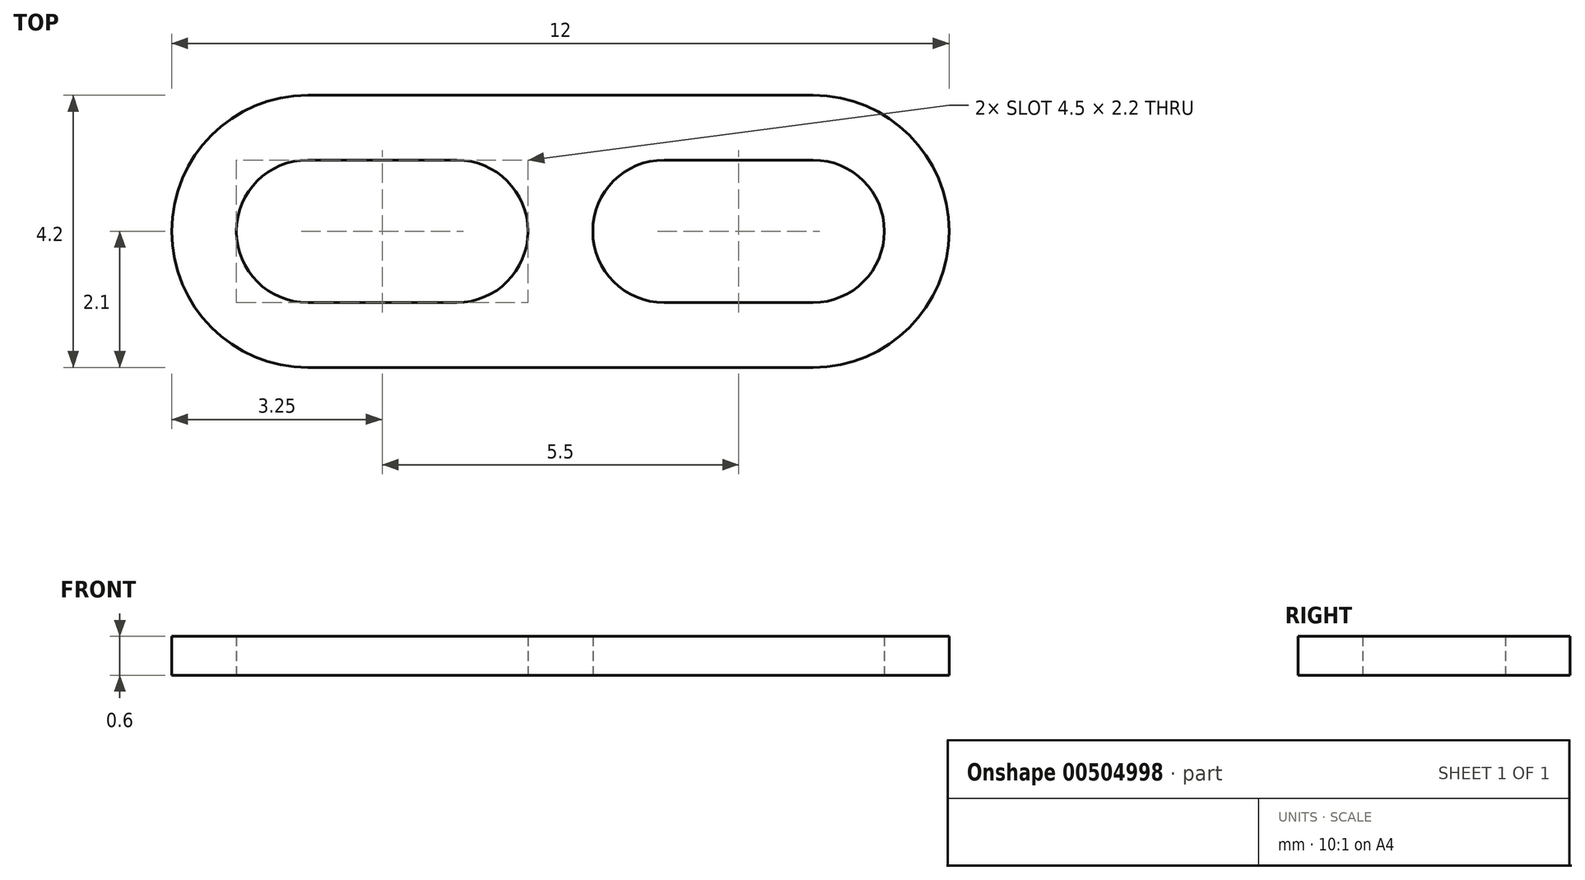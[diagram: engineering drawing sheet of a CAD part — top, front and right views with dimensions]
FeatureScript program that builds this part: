
annotation { "Feature Type Name" : "Feature", "Feature Type Description" : "" }
export const myFeature = defineFeature(function(context is Context, id is Id, definition is map)
    precondition{}
    {
        {
            var Q0;
            Q0=qCreatedBy(makeId("Top.planeOp"),FACE);
            var sketch = newSketch(context, id + "F0", { "sketchPlane" : qUnion([Q0])});
            skLineSegment(sketch, "E0.bottom", {"start": v(-3.9, 2) * mm, "end": v(3.9, 2) * mm});
            skLineSegment(sketch, "E0.top", {"start": v(-3.9, -2.2) * mm, "end": v(3.9, -2.2) * mm});
            skLineSegment(sketch, "E0.left", {"start": v(-6, -0.1) * mm, "end": v(-6, -0.1) * mm});
            skLineSegment(sketch, "E0.right", {"start": v(6, -0.1) * mm, "end": v(6, -0.1) * mm});
            skPoint(sketch, "E0.middle", {"position": v(0, 0) * mm});
            skPoint(sketch, "E1.visualSharp", {"position": v(-6, 2) * mm});
            skLineSegment(sketch, "E1.filletArc", {"start": v(-6, 2) * mm, "end": v(-6, 2) * mm});
            skLineSegment(sketch, "E2.filletArc", {"start": v(-6, -2.2) * mm, "end": v(-6, -2.2) * mm});
            skPoint(sketch, "E3.visualSharp", {"position": v(6, 2) * mm});
            skLineSegment(sketch, "E3.filletArc", {"start": v(6, 2) * mm, "end": v(6, 2) * mm});
            skLineSegment(sketch, "E4.filletArc", {"start": v(6, -2.2) * mm, "end": v(6, -2.2) * mm});
            skLineSegment(sketch, "E5.bottom", {"start": v(-3.9, 1) * mm, "end": v(-1.6, 1) * mm});
            skLineSegment(sketch, "E5.top", {"start": v(-3.9, -1.2) * mm, "end": v(-1.6, -1.2) * mm});
            skLineSegment(sketch, "E5.left", {"start": v(-5, -0.1) * mm, "end": v(-5, -0.1) * mm});
            skLineSegment(sketch, "E5.right", {"start": v(-0.5, -0.1) * mm, "end": v(-0.5, -0.1) * mm});
            skLineSegment(sketch, "E6.bottom", {"start": v(1.6, 1) * mm, "end": v(3.9, 1) * mm});
            skLineSegment(sketch, "E6.top", {"start": v(1.6, -1.2) * mm, "end": v(3.9, -1.2) * mm});
            skLineSegment(sketch, "E6.left", {"start": v(0.5, -0.1) * mm, "end": v(0.5, -0.1) * mm});
            skLineSegment(sketch, "E6.right", {"start": v(5, -0.1) * mm, "end": v(5, -0.1) * mm});
            skPoint(sketch, "E7.visualSharp", {"position": v(-5, 1) * mm});
            skArc(sketch, "E7.filletArc", {"start": v(-3.9, 1) * mm, "mid": v(-4.68, 0.68) * mm, "end": v(-5, -0.1) * mm});
            skPoint(sketch, "E8.visualSharp", {"position": v(-5, -1.2) * mm});
            skArc(sketch, "E8.filletArc", {"start": v(-5, -0.1) * mm, "mid": v(-4.68, -0.88) * mm, "end": v(-3.9, -1.2) * mm});
            skPoint(sketch, "E9.visualSharp", {"position": v(-0.5, -1.2) * mm});
            skArc(sketch, "E9.filletArc", {"start": v(-1.6, -1.2) * mm, "mid": v(-0.82, -0.88) * mm, "end": v(-0.5, -0.1) * mm});
            skPoint(sketch, "E10.visualSharp", {"position": v(-0.5, 1) * mm});
            skArc(sketch, "E10.filletArc", {"start": v(-0.5, -0.1) * mm, "mid": v(-0.82, 0.68) * mm, "end": v(-1.6, 1) * mm});
            skPoint(sketch, "E11.visualSharp", {"position": v(0.5, 1) * mm});
            skArc(sketch, "E11.filletArc", {"start": v(1.6, 1) * mm, "mid": v(0.82, 0.68) * mm, "end": v(0.5, -0.1) * mm});
            skPoint(sketch, "E12.visualSharp", {"position": v(0.5, -1.2) * mm});
            skArc(sketch, "E12.filletArc", {"start": v(0.5, -0.1) * mm, "mid": v(0.82, -0.88) * mm, "end": v(1.6, -1.2) * mm});
            skPoint(sketch, "E13.visualSharp", {"position": v(5, 1) * mm});
            skArc(sketch, "E13.filletArc", {"start": v(5, -0.1) * mm, "mid": v(4.68, 0.68) * mm, "end": v(3.9, 1) * mm});
            skPoint(sketch, "E14.visualSharp", {"position": v(5, -1.2) * mm});
            skArc(sketch, "E14.filletArc", {"start": v(3.9, -1.2) * mm, "mid": v(4.68, -0.88) * mm, "end": v(5, -0.1) * mm});
            skArc(sketch, "E15.filletArc", {"start": v(-3.9, 2) * mm, "mid": v(-5.38, 1.38) * mm, "end": v(-6, -0.1) * mm});
            skArc(sketch, "E16.filletArc", {"start": v(-6, -0.1) * mm, "mid": v(-5.38, -1.58) * mm, "end": v(-3.9, -2.2) * mm});
            skArc(sketch, "E17.filletArc", {"start": v(6, -0.1) * mm, "mid": v(5.38, 1.38) * mm, "end": v(3.9, 2) * mm});
            skArc(sketch, "E18.filletArc", {"start": v(3.9, -2.2) * mm, "mid": v(5.38, -1.58) * mm, "end": v(6, -0.1) * mm});
            skSolve(sketch);
        }
        {
            var Q0;
            Q0=makeQuery(id+"F0.imprint","IMPRINT",FACE,{"disambiguationData":[TD([[makeQuery(id+"F0.imprint","IMPRINT",EDGE,{"derivedFrom":sQuery(id+"F0.wireOp",EDGE,"E0.bottom")}),-1.0]])]});
            extrude(context, id + "F1", {"entities" : qUnion([Q0]), "depth" : 0.6 * mm});
        }
    });
